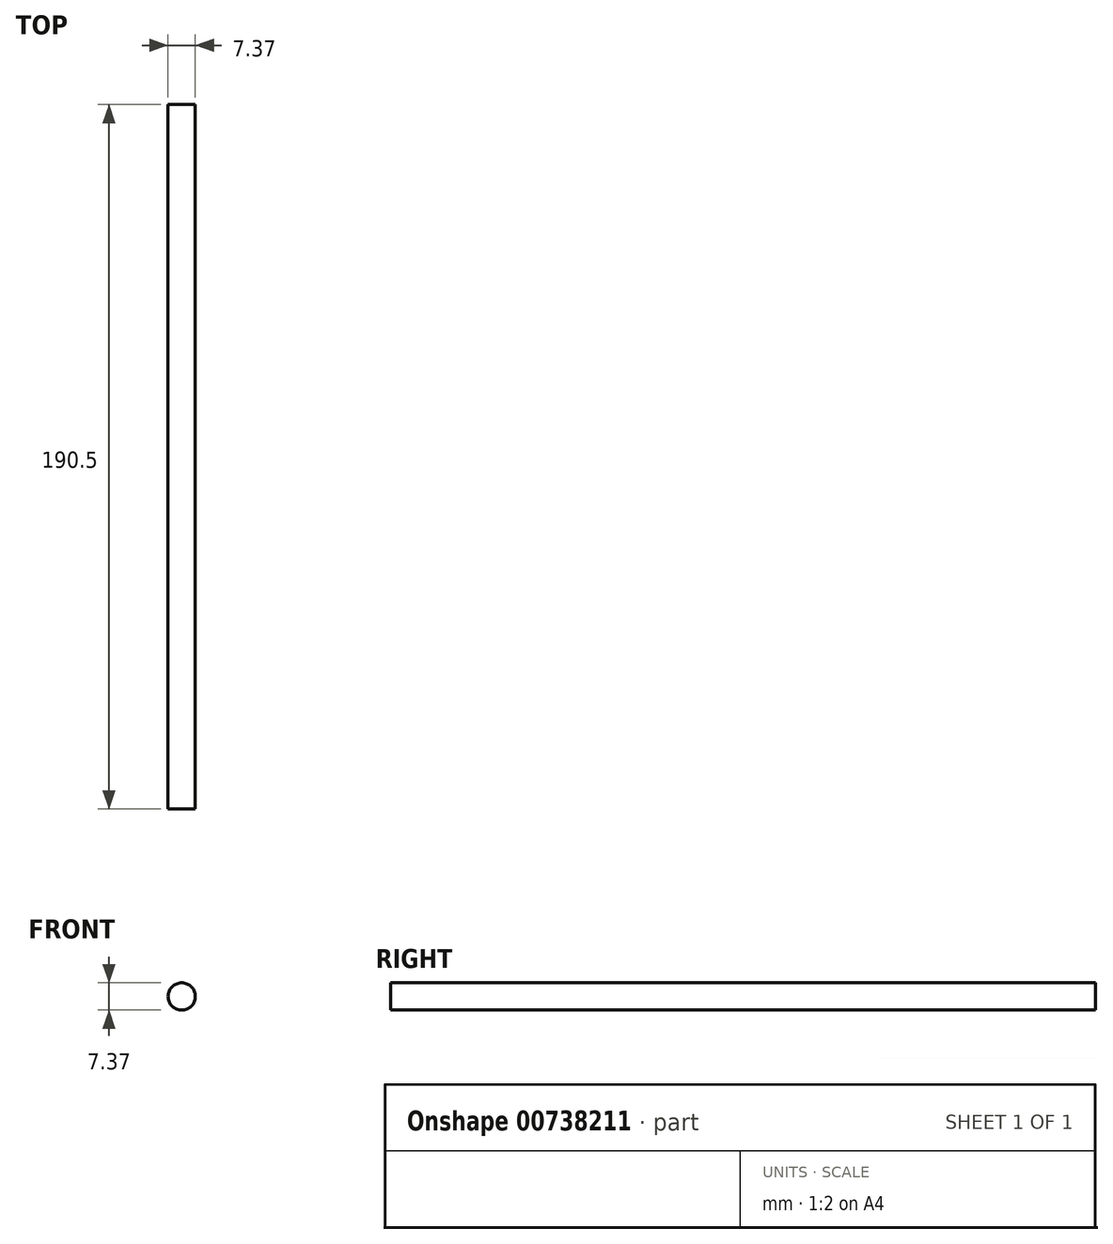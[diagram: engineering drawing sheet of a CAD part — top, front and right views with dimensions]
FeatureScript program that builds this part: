
annotation { "Feature Type Name" : "Feature", "Feature Type Description" : "" }
export const myFeature = defineFeature(function(context is Context, id is Id, definition is map)
    precondition{}
    {
        {
            var Q0;
            Q0=qCreatedBy(makeId("Front.planeOp"),FACE);
            var sketch = newSketch(context, id + "F0", { "sketchPlane" : qUnion([Q0])});
            skCircle(sketch, "E0", {"center": v(-40.38, 28) * mm, "radius": 3.68 * mm});
            skSolve(sketch);
        }
        {
            var Q0;
            Q0 = qSketchRegion(id + "F0", true);
            extrude(context, id + "F1", {"entities" : qUnion([Q0]), "depth" : 190.5 * mm, "offsetDistance" : 25.4 * mm});
        }
    });
